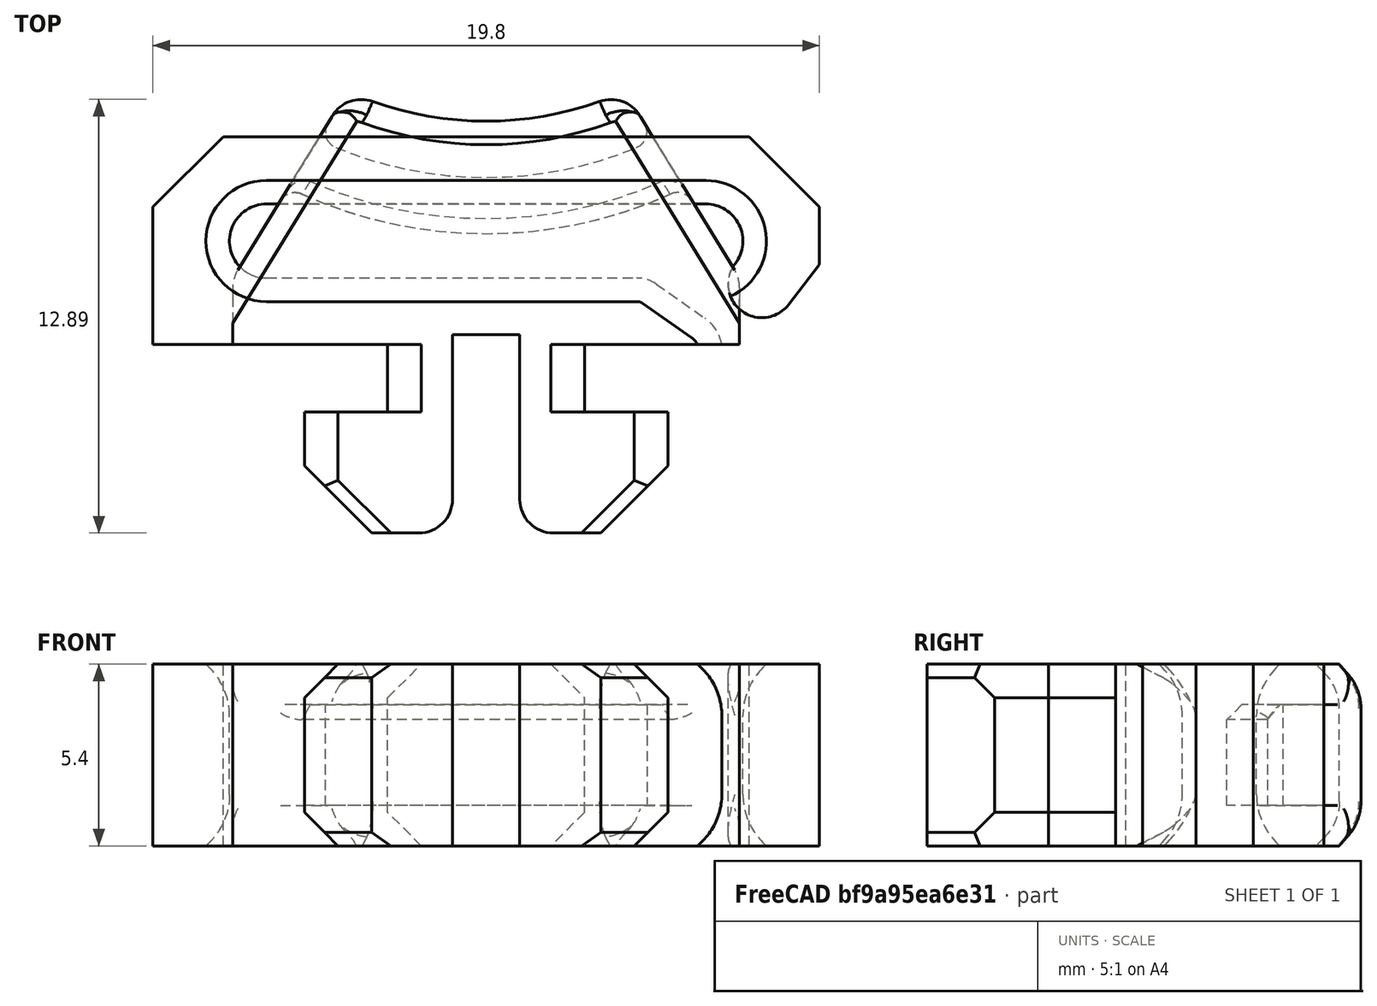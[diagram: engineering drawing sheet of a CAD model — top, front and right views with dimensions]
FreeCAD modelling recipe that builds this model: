
FCSTD DOCUMENT  (FreeCAD 0.18R16146 (Git))
Label: cable-clip
License: Other
LicenseURL: GPL3
objects: Part::Feature×15, Part::Box×4, Part::MultiCommon×3, Part::MultiFuse×3, Part::Cut×1
note: 26 computed .brp shape members not serialized (recipe doc carries the construction recipe); baked Part::Feature solids carry a one-line shape summary decoded from their .brp

FEATURE [Part::Feature] Part__Feature084001  label="cable_clip_lcd v008"
  Placement = pos=(-6,-5,-1) rot=(0.57735,0.57735,0.57735;2.0944rad)
  shape: bbox 19.81 x 12.04 x 5.879 mm, 79 faces (baked)
FEATURE [Part::Box] Box  label="Cube"
  AttacherType = Attacher::AttachEngine3D
  Height = 10
  Length = 22
  Placement = pos=(-11.5,-1.8,0) rot=(0,0,1;0rad)
  Width = 0.2
FEATURE [Part::Box] Box001  label="Cube001"
  AttacherType = Attacher::AttachEngine3D
  Height = 10
  Length = 22
  Placement = pos=(-11.5,0.2,0) rot=(0,0,1;0rad)
  Width = 10
FEATURE [Part::Feature] Part__Feature084002  label="cable_clip_lcd v009"
  Placement = pos=(-6,-5,-1) rot=(0.57735,0.57735,0.57735;2.0944rad)
  shape: bbox 19.81 x 12.04 x 5.879 mm, 79 faces (baked)
FEATURE [Part::MultiCommon] Common
  Shapes = -> [Box001,Part__Feature084002]
FEATURE [Part::Feature] Part__Feature084003  label="cable_clip_lcd v010"
  Placement = pos=(-6,-5,-1) rot=(0.57735,0.57735,0.57735;2.0944rad)
  shape: bbox 19.81 x 12.04 x 5.879 mm, 79 faces (baked)
FEATURE [Part::Box] Box002  label="Cube002"
  AttacherType = Attacher::AttachEngine3D
  Height = 10
  Length = 22
  Placement = pos=(-11.5,-11.8,0) rot=(0,0,1;0rad)
  Width = 10
FEATURE [Part::MultiCommon] Common001
  Shapes = -> [Box002,Part__Feature084003]
FEATURE [Part::MultiCommon] Common002
  Shapes = -> [Box,Part__Feature084001]
FEATURE [Part::Feature] Common002001  label="Common003"
  shape: bbox 5.85 x 0.2 x 5.4 mm, 16 faces, 2 solids (baked)
FEATURE [Part::Feature] Common002002  label="Common004"
  Placement = pos=(0,0.2,0) rot=(0,0,1;0rad)
  shape: bbox 5.85 x 0.2 x 5.4 mm, 16 faces, 2 solids (baked)
FEATURE [Part::Feature] Common002003  label="Common005"
  Placement = pos=(0,0.4,0) rot=(0,0,1;0rad)
  shape: bbox 5.85 x 0.2 x 5.4 mm, 16 faces, 2 solids (baked)
FEATURE [Part::Feature] Common002004  label="Common006"
  Placement = pos=(0,0.6,0) rot=(0,0,1;0rad)
  shape: bbox 5.85 x 0.2 x 5.4 mm, 16 faces, 2 solids (baked)
FEATURE [Part::Feature] Common002005  label="Common007"
  Placement = pos=(0,0.8,0) rot=(0,0,1;0rad)
  shape: bbox 5.85 x 0.2 x 5.4 mm, 16 faces, 2 solids (baked)
FEATURE [Part::Feature] Common002006  label="Common008"
  Placement = pos=(0,1,0) rot=(0,0,1;0rad)
  shape: bbox 5.85 x 0.2 x 5.4 mm, 16 faces, 2 solids (baked)
FEATURE [Part::Feature] Common002007  label="Common009"
  Placement = pos=(0,1.2,0) rot=(0,0,1;0rad)
  shape: bbox 5.85 x 0.2 x 5.4 mm, 16 faces, 2 solids (baked)
FEATURE [Part::Feature] Common002008  label="Common010"
  Placement = pos=(0,1.4,0) rot=(0,0,1;0rad)
  shape: bbox 5.85 x 0.2 x 5.4 mm, 16 faces, 2 solids (baked)
FEATURE [Part::Feature] Common002009  label="Common011"
  Placement = pos=(0,1.6,0) rot=(0,0,1;0rad)
  shape: bbox 5.85 x 0.2 x 5.4 mm, 16 faces, 2 solids (baked)
FEATURE [Part::Feature] Common002010  label="Common012"
  Placement = pos=(0,1.8,0) rot=(0,0,1;0rad)
  shape: bbox 5.85 x 0.2 x 5.4 mm, 16 faces, 2 solids (baked)
FEATURE [Part::Feature] Part__Feature089001  label="cable_clip_vertical v008"
  shape: bbox 15.57 x 12.94 x 5.775 mm, 77 faces (baked)
FEATURE [Part::Box] Box003  label="Cube003"
  AttacherType = Attacher::AttachEngine3D
  Height = 10
  Length = 16
  Placement = pos=(-7.6,-9.8,0) rot=(0,0,1;0rad)
  Width = 10
FEATURE [Part::Cut] Cut
  Base = -> Part__Feature089001
  Tool = -> Box003
FEATURE [Part::MultiFuse] Fusion
  Shapes = -> [Common001,Common002006,Common002005,Common002009,Common002002,Common002007,Common002010,Common002004,Common002008,Common002001,Common002003,Common002]
FEATURE [Part::Feature] Fusion001
  shape: bbox 10.8 x 5.6 x 5.4 mm, 146 faces, 2 solids (baked)
FEATURE [Part::MultiFuse] Fusion002  label="LCD-clip"
  Shapes = -> [Common,Fusion001]
FEATURE [Part::MultiFuse] Fusion003
  Shapes = -> [Cut,Fusion]
